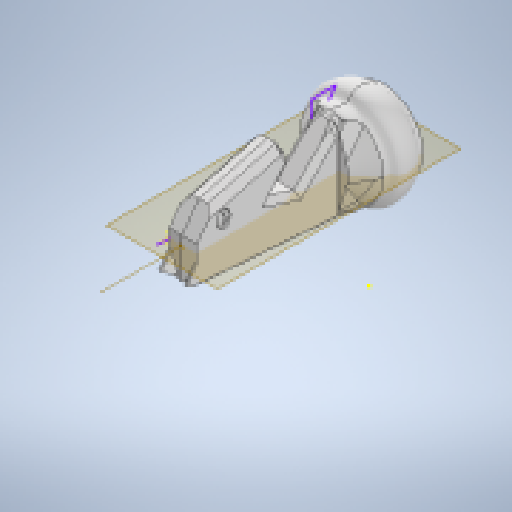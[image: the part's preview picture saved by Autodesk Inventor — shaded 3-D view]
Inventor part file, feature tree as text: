
AUTODESK INVENTOR PART (.ipt)
format: ipt  version: 2024.1 (Build 281209000, 209)  size: 1,121,792 bytes
history: native  units: mm
features: sketch x16, extrude x11, chamfer x10, fillet x10, projected_geometry x6, other x3, mirror x2, sweep x2, revolve x1, plane x1
ambient origin geometry x8: Origin, YZ Plane, XZ Plane, XY Plane, X Axis, Y Axis, Z Axis, Center Point
bodies: Solid1 (feature_tree)
feature tree (62):
  extrude  "Extrusion1"  Depth=3.0mm TaperAngle=0.0deg
  other  "Work Axis1"
  extrude  "Extrusion2"  Depth=14.3mm
  revolve  "Revolution1"  [1 undecoded]
  chamfer  "Chamfer7"  Distance=0.1mm Angle=45.0deg
  extrude  "Extrusion12"  Depth=7.5mm
  extrude  "Extrusion13"  Depth=2.0mm
  extrude  "Extrusion14"  TaperAngle=0.0deg  [1 undecoded]
  fillet  "Fillet9"  Radius=0.679639mm
  fillet  "Fillet10"  Radius=10.0mm
  extrude  "Extrusion15"  Depth=0.5mm
  chamfer  "Chamfer8"  Distance=1.6mm
  sketch  "Sketch23"  dims[d155=5.0mm d156=-1.047198mm d157=0.0mm d158=0.0mm d159=0.679639mm d160=10.0mm d161=-2.443461mm]
  extrude  "Extrusion16"  Depth=1.0mm
  chamfer  "Chamfer9"  Distance=1.0mm
  chamfer  "Chamfer10"  Distance=0.4mm Angle=45.0deg
  extrude  "Extrusion17"  Depth=0.8mm
  fillet  "Fillet11"  Radius=1.3mm
  fillet  "Fillet12"  Radius=1.0mm
  extrude  "Extrusion18"  Depth=0.1mm
  chamfer  "Chamfer11"  [1 undecoded]
  chamfer  "Chamfer12"  Distance=10.0mm
  chamfer  "Chamfer13"  Distance=0.2mm Angle=45.0deg
  extrude  "Extrusion19"  Depth=1.0mm TaperAngle=45.0deg
  chamfer  "Chamfer15"  Distance=0.3mm Angle=45.0deg
  extrude  "Extrusion20"  Depth=1.0mm TaperAngle=0.0deg
  mirror  "Mirror1"
  fillet  "Fillet13"  Radius=1.0mm
  other  "Work Axis14"
  plane  "Work Plane10"
  fillet  "Fillet14"  [1 undecoded]
  sketch  "Sketch35"  dims[d180=1.5mm d181=1.2mm d182=45.0deg d183=0.8mm d184=1.3mm d185=1.0mm d186=0.0mm]
  sweep  "Sweep3"
  sweep  "Sweep4"
  fillet  "Fillet15"  [1 undecoded]
  mirror  "Mirror2"
  chamfer  "Chamfer19"  [1 undecoded]
  fillet  "Fillet16"  Radius=8.0mm
  fillet  "Fillet17"  Radius=8.0mm
  fillet  "Fillet19"  Radius=10.0mm
  chamfer  "Chamfer20"  Distance=1.5mm Angle=45.0deg
  sketch  "Sketch1"  dims[d0=10.0mm d1=3.0mm d2=0.0mm]
  sketch  "Sketch2"  dims[d5=360.0deg d6=14.3mm]
  sketch  "Sketch3"  dims[d7=3.0mm d8=0.0mm d135=0.8mm]
  projected_geometry  "Projected Loop1"
  projected_geometry  "Projected Loop3"
  sketch  "Sketch18"  dims[d146=9.25mm]
  projected_geometry  "Projected Loop4"
  sketch  "Sketch20"  dims[d147=1.0mm d148=0.1mm d149=1.0mm d150=45.0deg]
  projected_geometry  "Projected Loop7"
  sketch  "Sketch21"  dims[d151=36.0mm d152=7.5mm]
  projected_geometry  "Projected Loop8"
  sketch  "Sketch22"  dims[d153=2.5mm d154=2.0mm]
  sketch  "Sketch24"  dims[d162=0.5mm d163=0.5mm]
  sketch  "Sketch25"  dims[d164=3.5mm]
  projected_geometry  "Projected Loop9"
  sketch  "Sketch26"  dims[d165=1.8mm d166=1.6mm d167=0.0mm]
  sketch  "Sketch27"  dims[d168=3.25mm d169=2.0mm d170=45.0deg d171=1.0mm]
  sketch  "Sketch28"  dims[d172=1.4mm d175=1.0mm d176=0.0mm d177=0.4mm d178=2.0mm d179=45.0deg]
  other  "Work Point4"
  sketch  "Sketch36"  dims[d187=0.6mm d188=0.1mm d189=0.0mm d190=0.0mm]
  sketch  "Sketch38"  dims[d191=20.0mm d192=10.0mm d193=0.2mm d194=1.2mm d195=45.0deg d196=1.0mm d197=1.2mm d198=45.0deg d199=0.3mm d200=1.2mm d201=45.0deg d202=1.0mm d203=0.0mm d207=1.0mm d208=1.2mm d209=45.0deg d210=0.0mm d211=0.0mm d212=0.8mm d221=0.5mm d230=0.0mm d231=0.0mm d234=0.0mm d235=0.0mm d236=8.0mm d237=8.0mm d238=10.0mm d239=1.5mm d240=2.0mm d241=45.0deg d242=1.2mm d243=1.2mm d245=2.0mm d246=5.803797mm d247=2.894102mm d248=1.1mm d249=2.0mm d250=45.0deg d98=0.0mm d99=0.0mm d100=0.0mm d101=0.0mm]
note: 6 required parameter values undecoded (feature->parameter linkage not recoverable at this tier; creation-order binding heuristic only, values carry confidence <= 0.55)